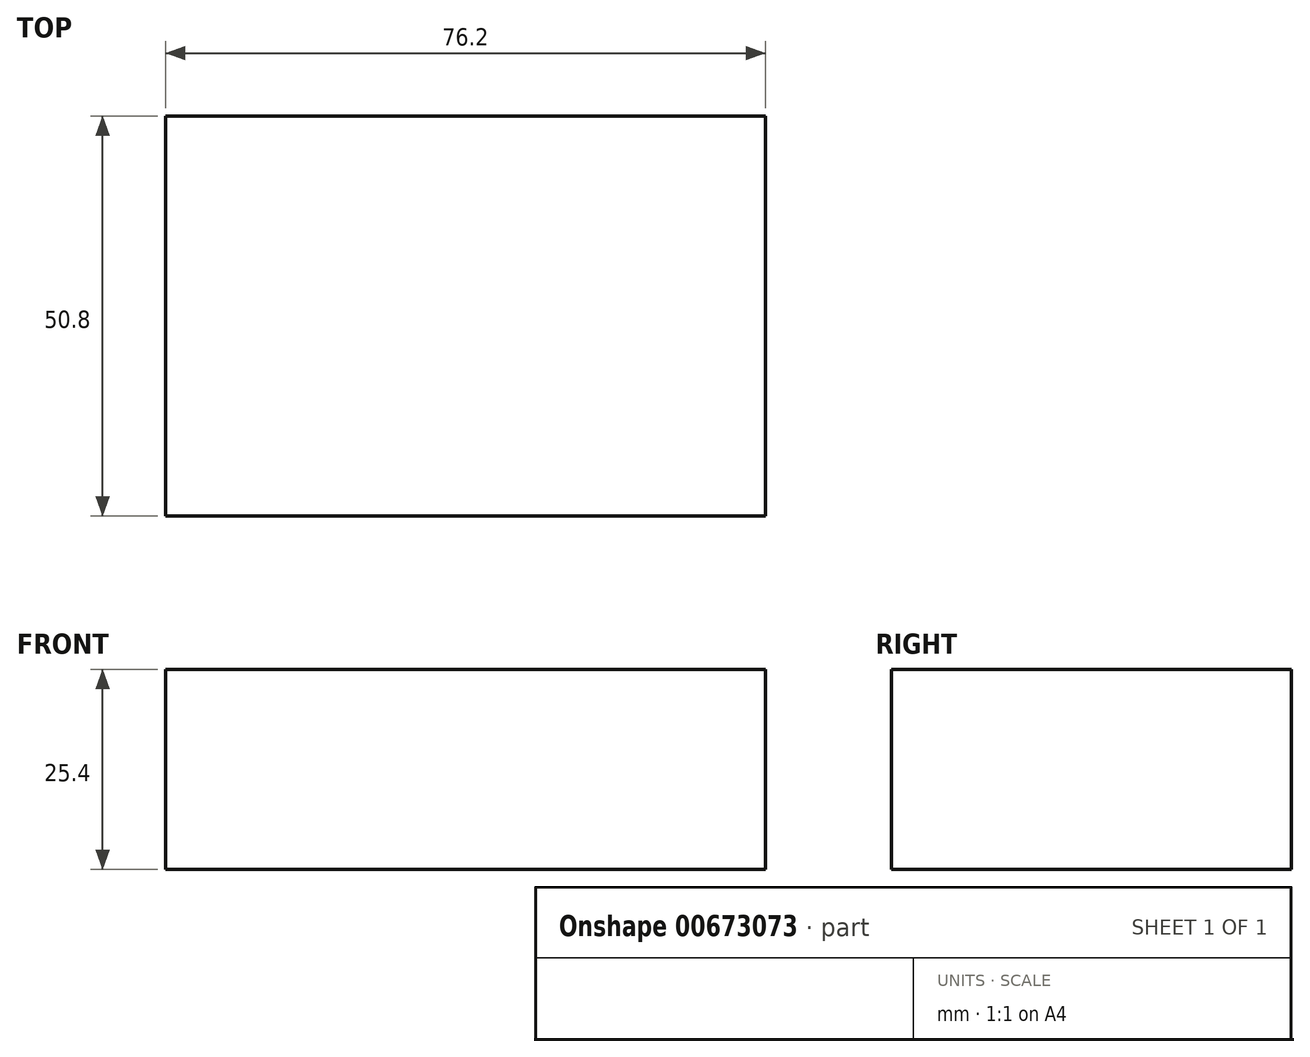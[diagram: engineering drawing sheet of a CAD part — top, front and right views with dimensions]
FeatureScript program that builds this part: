
annotation { "Feature Type Name" : "Feature", "Feature Type Description" : "" }
export const myFeature = defineFeature(function(context is Context, id is Id, definition is map)
    precondition{}
    {
        {
            var Q0;
            Q0=qCreatedBy(makeId("Top.planeOp"),FACE);
            var sketch = newSketch(context, id + "F0", { "sketchPlane" : qUnion([Q0])});
            skLineSegment(sketch, "E0.bottom", {"start": v(0, 0) * mm, "end": v(-76.2, 0) * mm});
            skLineSegment(sketch, "E0.top", {"start": v(0, 50.8) * mm, "end": v(-76.2, 50.8) * mm});
            skLineSegment(sketch, "E0.left", {"start": v(0, 0) * mm, "end": v(0, 50.8) * mm});
            skLineSegment(sketch, "E0.right", {"start": v(-76.2, 0) * mm, "end": v(-76.2, 50.8) * mm});
            skSolve(sketch);
        }
        {
            var Q0;
            Q0 = qSketchRegion(id + "F0", true);
            extrude(context, id + "F1", {"entities" : qUnion([Q0]), "depth" : 25.4 * mm, "offsetDistance" : 25.4 * mm});
        }
    });
